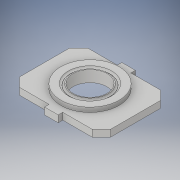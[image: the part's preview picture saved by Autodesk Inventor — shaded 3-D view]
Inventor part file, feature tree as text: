
AUTODESK INVENTOR PART (.ipt)
format: ipt  version: 2019 (Build 230136000, 136)  size: 200,704 bytes
history: native  units: mm
features: extrude x6, sketch x6, chamfer x1, fillet x1
ambient origin geometry x8: Origin, YZ Plane, XZ Plane, XY Plane, X Axis, Y Axis, Z Axis, Center Point
bodies: Solid1 (feature_tree)
feature tree (14):
  extrude  "Extrusion1"  Depth=40.0mm
  extrude  "Extrusion2"  Depth=3.0mm
  extrude  "Extrusion3"  Depth=15.0mm
  extrude  "Extrusion4"  Depth=2.0mm
  chamfer  "Chamfer1"  Distance=2.0mm
  extrude  "Extrusion5"  Depth=5.0mm
  extrude  "Extrusion6"  Depth=0.8mm
  fillet  "Fillet1"  Radius=10.0mm
  sketch  "Sketch1"  dims[d0=30.0mm d1=40.0mm]
  sketch  "Sketch2"  dims[d2=3.0mm d3=0.0mm d4=15.0mm]
  sketch  "Sketch3"  dims[d5=20.0mm d6=15.0mm]
  sketch  "Sketch4"  dims[d7=3.0mm d8=0.0mm d9=25.6mm d10=2.0mm d11=0.0mm]
  sketch  "Sketch5"  dims[d12=5.0mm d13=5.0mm]
  sketch  "Sketch6"  dims[d14=5.0mm d15=15.0mm d16=10.0mm d17=10.0mm d18=15.0mm d19=15.0mm d20=15.0mm d21=10.0mm d22=10.0mm d23=2.0mm d24=0.0mm d25=4.0mm d26=2.0mm d27=45.0deg d28=6.0mm d29=17.0mm d30=2.0mm d31=6.0mm d32=17.0mm d33=2.0mm d34=0.0mm d35=2.0mm d36=3.0mm d37=0.0mm d38=15.8mm d39=19.1mm d40=0.7mm d41=0.0mm d42=0.8mm]
